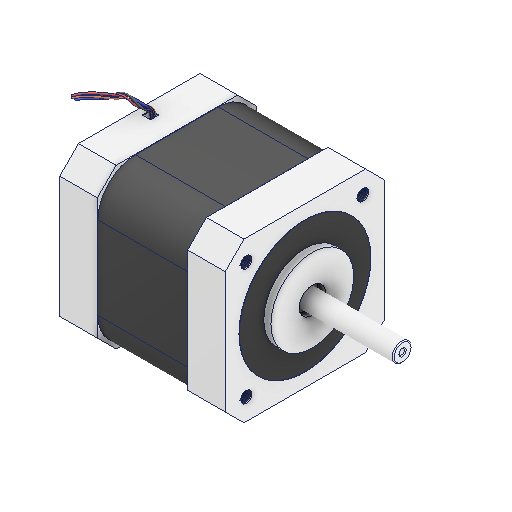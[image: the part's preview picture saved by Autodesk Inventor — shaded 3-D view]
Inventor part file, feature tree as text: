
AUTODESK INVENTOR PART (.ipt)
format: ipt  version: 2025.1 (Build 291241000, 241)  size: 923,136 bytes
history: native  units: mm
features: other x1, fillet x1
ambient origin geometry x8: Origin, YZ Plane, XZ Plane, XY Plane, X Axis, Y Axis, Z Axis, Center Point
bodies: Body1 (feature_tree)
feature tree (2):
  other  "Bryła1"
  fillet  "Fillet2"  [1 undecoded]
note: 1 required parameter value undecoded (feature->parameter linkage not recoverable at this tier; creation-order binding heuristic only, values carry confidence <= 0.55)
